# Revit family: 34. Plumbing_Fixtures_Grohe_Concealed_valve_29032000
name_source: partatom
category: Pipe Accessories
revit_build: Autodesk Revit 2014 (Build: 20130308_1515(x64)
units: mm (PartAtom-declared; Revit-internal decimal feet)

## types (1)
- Concealed valve - 29032000
    Adjustable Depth = 43 mm  [stored 0.141076 ft]
    Assembly Code = D20
    AssetType = Fixed
    Body Curve Centre = 34 mm
    Body Radius = 55 mm  [stored 0.180446 ft]
    Body Width = 40 mm  [stored 0.131234 ft]
    Cap Material = UHMW, Black
    ClassificationName = Uniclass2015
    ClassificationValue = Pr_65_54_40_13
    Color = Bronze
    Connection Diameter = 21 mm
    Connection Size Radius = 11 mm
    Description = Concealed valve, pre-assembled headpart 1/2", threaded union 1/2", installation depth adjustable 43 - 91 mm DR-brass min. recommended pressure 1.0 bar model
    DocumentationInstallationGuide = http://cdn08.grohe.com
    DocumentationLiterature = http://cdn08.grohe.com
    DocumentationTechnical = http://cdn08.grohe.com
    Ecojoy = No
    ExpectedLife = 0
    Features = Installation depth adjustable 43 - 91 mm
    Finish = No finish
    Handle Dia = 55 mm  [stored 0.180446 ft]
    Handle Height = 80 mm  [stored 0.262467 ft]
    K Coefficient = 0
    Keynote = S90/620
    Loss Method = K Coefficient
    Manufacturer = Grohe AG
    Material = DR-brass
    Model = Concealed valve - 29032000
    ModelNumber = 29032000
    NBSDescription = Check valves
    NBSObjectName = Check valves
    NBSReference = 90-15-40/323
    Nut Diameter = 38 mm
    Nut Thickness = 13 mm
    Product Page Link = http://www.grohe.co.uk
    ProductionYear = 2015
    Spare Parts List = http://www.grohe.co.uk
    TagNumber = Concealed valve - 29032000
    Type Comments = Grohe Ondus Concealed valve
    TypeName = Concealed valve - 29032000
    URL = http://www.grohe.com
    Valve Material = Red Brass Rg5
    WarrantyDurationUnit = Years
    _BIMspec_GUID = 0
    _current revision = 1
    _distributed by = www.bimstore.co.uk

note: [stored X ft] marks values corroborated as IEEE doubles in the binary element streams (Revit-internal decimal feet)

## geometry (parser evidence)
native form markers: Blend x8, Sweep x7
no freeform markers — native parametric forms only
